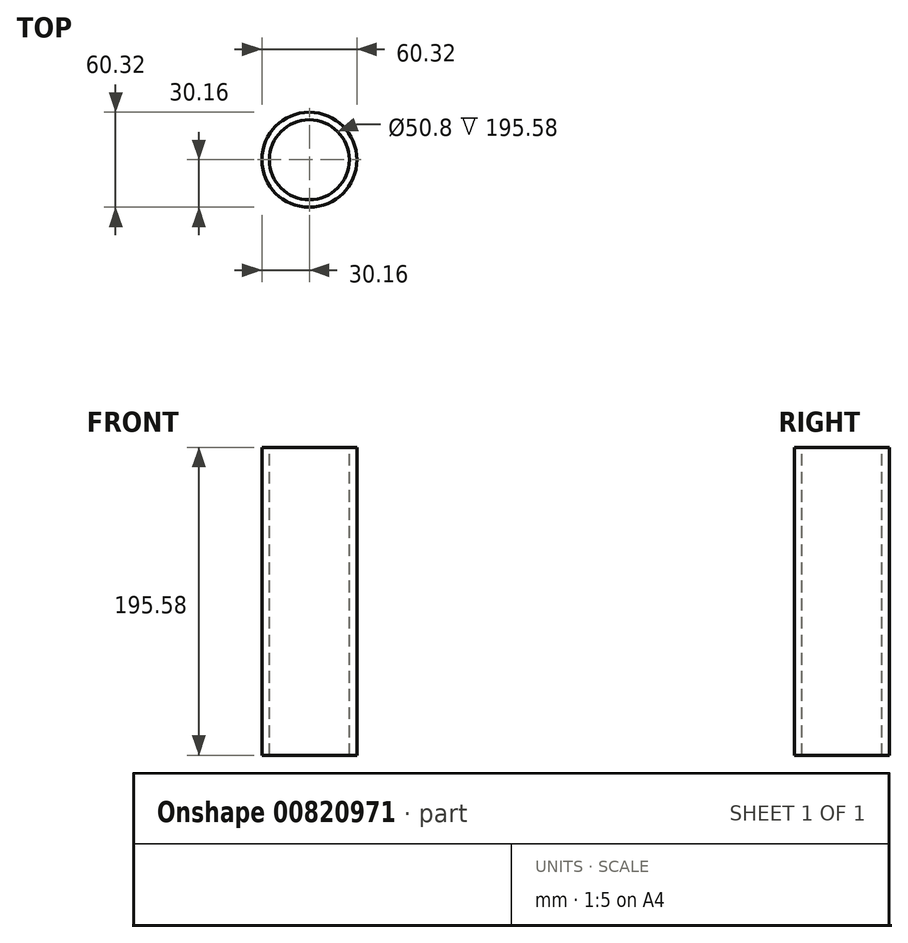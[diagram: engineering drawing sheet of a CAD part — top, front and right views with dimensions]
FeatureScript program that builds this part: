
annotation { "Feature Type Name" : "Feature", "Feature Type Description" : "" }
export const myFeature = defineFeature(function(context is Context, id is Id, definition is map)
    precondition{}
    {
        {
            var Q0;
            Q0=qCreatedBy(makeId("Top.planeOp"),FACE);
            var sketch = newSketch(context, id + "F0", { "sketchPlane" : qUnion([Q0])});
            skCircle(sketch, "E0", {"center": v(0, 0) * mm, "radius": 30.16 * mm});
            skCircle(sketch, "E1", {"center": v(0, 0) * mm, "radius": 25.4 * mm});
            skSolve(sketch);
        }
        {
            var Q0;
            Q0=qSketchRegion(id+"F0",true);
            extrude(context, id + "F1", {"entities" : qUnion([Q0]), "oppositeDirection" : true, "depth" : 195.58 * mm, "offsetDistance" : 25.4 * mm});
        }
    });
